# Revit family: Sanitary_Screens-Dividers_hansgrohe_60173XXX-CreekTide-Q-Urinal-division_NEW
name_source: partatom
category: Furniture
revit_build: Autodesk Revit 2018 (Build: 20170223_1515(x64)
units: mm (PartAtom-declared; Revit-internal decimal feet)

## family parameters
Always vertical = No
Cut with Voids When Loaded = No
OmniClass Number = 23.15.11.15.11
OmniClass Title = Toilet Compartments and Urinal Screens
Room Calculation Point = No
Shared = No
Work Plane-Based = Yes

## types (1)
- 450 White
    Always visible = Yes
    BIMobject category = Screens & Dividers
    Default Elevation = 1219.2 mm  [stored 4 ft]
    Description = CreekTide Q Urinal division
    Design country = Germany
    EAN code = 4059625478189
    Edition number = 1
    GTIN code = https://4059625478189
    IFC Classification = Furnishing Element
    Manufacturer = Hansgrohe
    Manufacturer country = Germany
    Manufacturer name = hansgrohe
    Masterformat 2014 Code = 10 21 00
    Masterformat 2014 Description = Compartments and Cubicles
    Material 1 = Hansgrohe - Ceramic - 450 White
    Model = 60173XXX
    OmniClass Code = 23-15 11 15 11
    OmniClass Description = Toilet Compartments and Urinal Screens
    Product Guid = 0efe297b-e336-4c63-98da-55d7875aeaa8
    Product SKU = 60173XXX
    Product data url = https://bimobject.com
    Product family = CreekTide Q
    Product group = Urinal division
    Product name = 60173XXX CreekTide Q Urinal division
    Product url = https://pro.hansgrohe.com
    QR code = https://bimobject.com
    UNSPSC Code = 30181506
    URL = https://www.hansgrohe.com
    Uniclass 2015 Code = Pr_40_20_93_74
    Uniclass 2015 Name = Urinal dividers
    Uniformat II Code = E2010
    Uniformat II Description = Fixed Furnishings
    Weight Net (Kg) = 15.4

note: [stored X ft] marks values corroborated as IEEE doubles in the binary element streams (Revit-internal decimal feet)

## geometry (parser evidence)
native form markers: Sweep x2
no freeform markers — native parametric forms only
